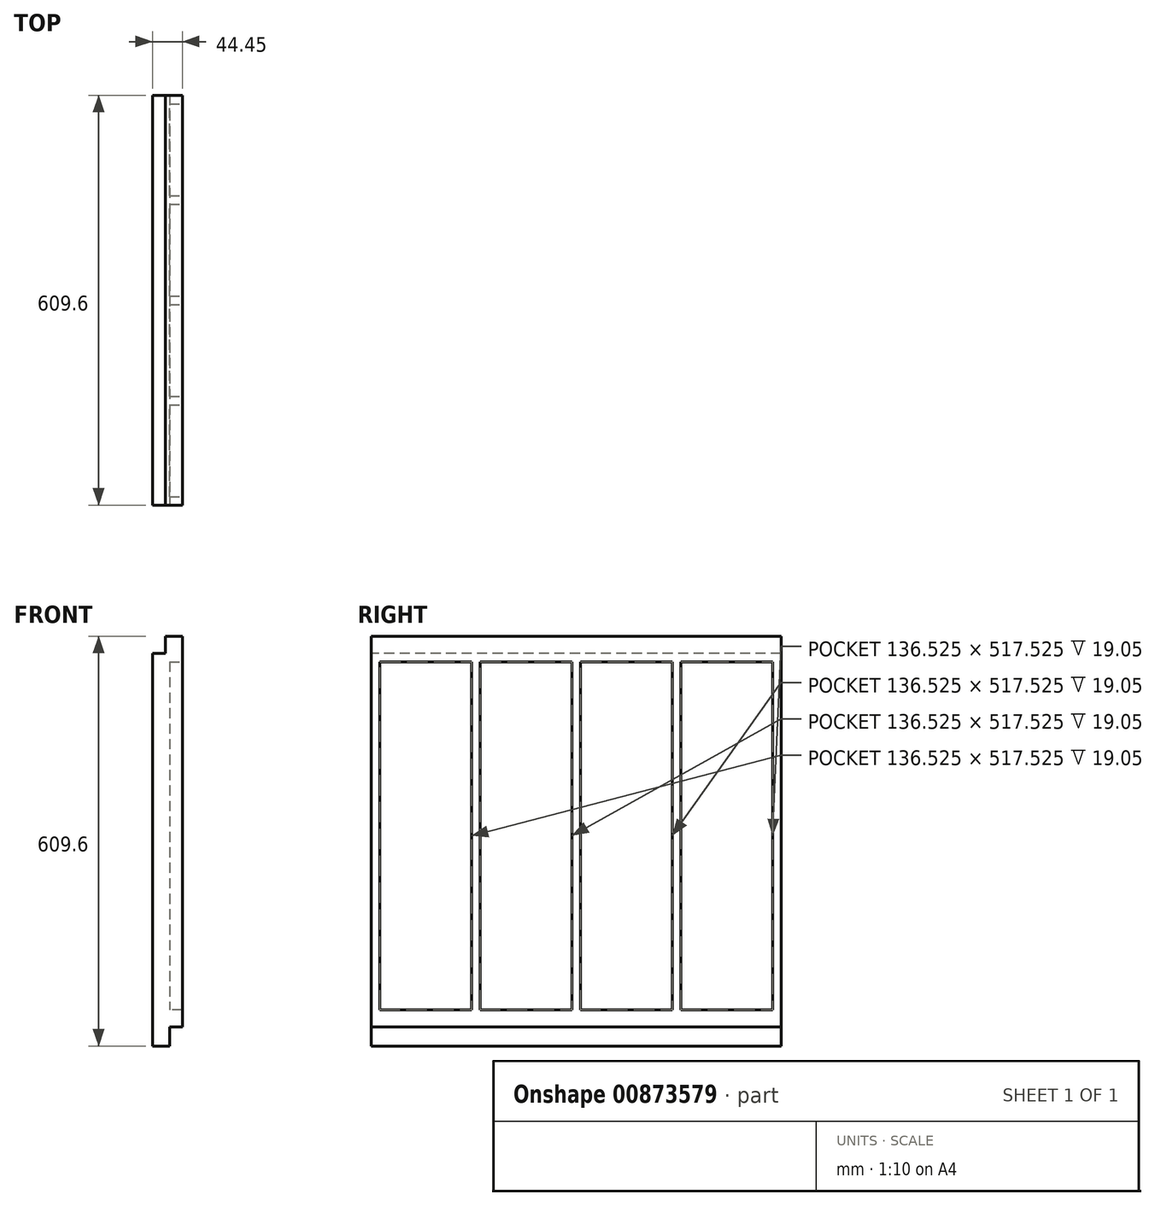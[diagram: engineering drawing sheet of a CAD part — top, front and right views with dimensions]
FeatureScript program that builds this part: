
annotation { "Feature Type Name" : "Feature", "Feature Type Description" : "" }
export const myFeature = defineFeature(function(context is Context, id is Id, definition is map)
    precondition{}
    {
        {
            var Q0;
            Q0=qCreatedBy(makeId("Top.planeOp"),FACE);
            var sketch = newSketch(context, id + "F0", { "sketchPlane" : qUnion([Q0])});
            skLineSegment(sketch, "E0.bottom", {"start": v(0, 0) * mm, "end": v(25.4, 0) * mm});
            skLineSegment(sketch, "E0.top", {"start": v(0, 609.6) * mm, "end": v(25.4, 609.6) * mm});
            skLineSegment(sketch, "E0.left", {"start": v(0, 0) * mm, "end": v(0, 609.6) * mm});
            skLineSegment(sketch, "E0.right", {"start": v(25.4, 12.7) * mm, "end": v(25.4, 149.23) * mm});
            skLineSegment(sketch, "E1", {"start": v(12.7, 648.7) * mm, "end": v(12.7, -109.72) * mm, "construction": true});
            skPoint(sketch, "E1.startSnap0", {"position": v(12.7, 609.6) * mm});
            skLineSegment(sketch, "E2.bottom", {"start": v(25.4, 0) * mm, "end": v(44.45, 0) * mm});
            skLineSegment(sketch, "E2.top", {"start": v(25.4, 12.7) * mm, "end": v(44.45, 12.7) * mm});
            skLineSegment(sketch, "E2.right", {"start": v(44.45, 0) * mm, "end": v(44.45, 12.7) * mm});
            skLineSegment(sketch, "E3.0.1.0", {"start": v(25.4, 161.93) * mm, "end": v(44.45, 161.93) * mm});
            skLineSegment(sketch, "E3.0.1.1", {"start": v(44.45, 149.23) * mm, "end": v(44.45, 161.93) * mm});
            skLineSegment(sketch, "E3.0.1.2", {"start": v(25.4, 149.23) * mm, "end": v(44.45, 149.23) * mm});
            skLineSegment(sketch, "E3.0.2.0", {"start": v(25.4, 311.15) * mm, "end": v(44.45, 311.15) * mm});
            skLineSegment(sketch, "E3.0.2.1", {"start": v(44.45, 298.45) * mm, "end": v(44.45, 311.15) * mm});
            skLineSegment(sketch, "E3.0.2.2", {"start": v(25.4, 298.45) * mm, "end": v(44.45, 298.45) * mm});
            skLineSegment(sketch, "E3.0.3.0", {"start": v(25.4, 460.38) * mm, "end": v(44.45, 460.38) * mm});
            skLineSegment(sketch, "E3.0.3.1", {"start": v(44.45, 447.68) * mm, "end": v(44.45, 460.38) * mm});
            skLineSegment(sketch, "E3.0.3.2", {"start": v(25.4, 447.68) * mm, "end": v(44.45, 447.68) * mm});
            skLineSegment(sketch, "E3.0.4.0", {"start": v(25.4, 609.6) * mm, "end": v(44.45, 609.6) * mm});
            skLineSegment(sketch, "E3.0.4.1", {"start": v(44.45, 596.9) * mm, "end": v(44.45, 609.6) * mm});
            skLineSegment(sketch, "E3.0.4.2", {"start": v(25.4, 596.9) * mm, "end": v(44.45, 596.9) * mm});
            skLineSegment(sketch, "E3.direction1", {"start": v(25.4, 12.7) * mm, "end": v(50.8, 12.7) * mm, "construction": true});
            skLineSegment(sketch, "E3.direction2", {"start": v(25.4, 12.7) * mm, "end": v(25.4, 149.22) * mm, "construction": true});
            skLineSegment(sketch, "E4.trimOffspring", {"start": v(25.4, 460.38) * mm, "end": v(25.4, 596.9) * mm});
            skLineSegment(sketch, "E5.trimOffspring", {"start": v(25.4, 311.15) * mm, "end": v(25.4, 447.68) * mm});
            skLineSegment(sketch, "E6.trimOffspring", {"start": v(25.4, 161.93) * mm, "end": v(25.4, 298.45) * mm});
            skSolve(sketch);
        }
        {
            var Q0;
            Q0 = qSketchRegion(id + "F0", true);
            extrude(context, id + "F1", {"entities" : qUnion([Q0]), "depth" : 609.6 * mm, "offsetDistance" : 25.4 * mm});
        }
        {
            var Q0;
            Q0=makeQuery(id+"F1.opExtrude","SWEPT_FACE",FACE,{"disambiguationData":[OSD([sQuery(id+"F0.wireOp",EDGE,"E0.bottom"),sQuery(id+"F0.wireOp",EDGE,"E2.bottom")])]});
            var sketch = newSketch(context, id + "F2", { "sketchPlane" : qUnion([Q0])});
            skLineSegment(sketch, "E7.bottom", {"start": v(0, 0) * mm, "end": v(50.8, 0) * mm});
            skLineSegment(sketch, "E7.top", {"start": v(0, 25.4) * mm, "end": v(50.8, 25.4) * mm});
            skLineSegment(sketch, "E7.left", {"start": v(0, 0) * mm, "end": v(0, 25.4) * mm});
            skLineSegment(sketch, "E7.right", {"start": v(50.8, 0) * mm, "end": v(50.8, 25.4) * mm});
            skSolve(sketch);
        }
        {
            var Q0;
            Q0 = qSketchRegion(id + "F2", true);
            extrude(context, id + "F3", {"entities" : qUnion([Q0]), "operationType" : NewBodyOperationType.ADD, "oppositeDirection" : true, "depth" : 609.6 * mm, "offsetDistance" : 25.4 * mm});
        }
        {
            var Q0;
            Q0=makeQuery(id+"F1.opExtrude","SWEPT_FACE",FACE,{"disambiguationData":[OSD([sQuery(id+"F0.wireOp",EDGE,"E0.bottom"),sQuery(id+"F0.wireOp",EDGE,"E2.bottom")])]});
            var sketch = newSketch(context, id + "F4", { "sketchPlane" : qUnion([Q0])});
            skLineSegment(sketch, "E8.bottom", {"start": v(0, 609.6) * mm, "end": v(25.4, 609.6) * mm});
            skLineSegment(sketch, "E8.top", {"start": v(0, 584.2) * mm, "end": v(25.4, 584.2) * mm});
            skLineSegment(sketch, "E8.left", {"start": v(0, 609.6) * mm, "end": v(0, 584.2) * mm});
            skLineSegment(sketch, "E8.right", {"start": v(25.4, 609.6) * mm, "end": v(25.4, 584.2) * mm});
            skSolve(sketch);
        }
        {
            var Q0;
            Q0 = qSketchRegion(id + "F4", true);
            extrude(context, id + "F5", {"entities" : qUnion([Q0]), "operationType" : NewBodyOperationType.REMOVE, "oppositeDirection" : true, "depth" : 609.6 * mm, "offsetDistance" : 25.4 * mm});
        }
        {
            var Q0;
            Q0=makeQuery(id+"F1.opExtrude","SWEPT_FACE",FACE,{"disambiguationData":[OSD([sQuery(id+"F0.wireOp",EDGE,"E0.bottom"),sQuery(id+"F0.wireOp",EDGE,"E2.bottom")])]});
            var sketch = newSketch(context, id + "F6", { "sketchPlane" : qUnion([Q0])});
            skLineSegment(sketch, "E9.bottom", {"start": v(50.8, 0) * mm, "end": v(25.4, 0) * mm});
            skLineSegment(sketch, "E9.top", {"start": v(50.8, 28.57) * mm, "end": v(25.4, 28.57) * mm});
            skLineSegment(sketch, "E9.left", {"start": v(50.8, 0) * mm, "end": v(50.8, 28.58) * mm});
            skLineSegment(sketch, "E9.right", {"start": v(25.4, 0) * mm, "end": v(25.4, 28.57) * mm});
            skSolve(sketch);
        }
        {
            var Q0;
            Q0 = qSketchRegion(id + "F6", true);
            extrude(context, id + "F7", {"entities" : qUnion([Q0]), "operationType" : NewBodyOperationType.REMOVE, "oppositeDirection" : true, "depth" : 609.6 * mm, "offsetDistance" : 25.4 * mm});
        }
        {
            var Q0;
            Q0=makeQuery(id+"F1.opExtrude","SWEPT_FACE",FACE,{"disambiguationData":[OSD([sQuery(id+"F0.wireOp",EDGE,"E0.bottom"),sQuery(id+"F0.wireOp",EDGE,"E2.bottom")])]});
            var sketch = newSketch(context, id + "F8", { "sketchPlane" : qUnion([Q0])});
            skLineSegment(sketch, "E10.bottom", {"start": v(25.4, 28.57) * mm, "end": v(44.45, 28.57) * mm});
            skLineSegment(sketch, "E10.top", {"start": v(25.4, 53.98) * mm, "end": v(44.45, 53.98) * mm});
            skLineSegment(sketch, "E10.left", {"start": v(25.4, 28.57) * mm, "end": v(25.4, 53.97) * mm});
            skLineSegment(sketch, "E10.right", {"start": v(44.45, 28.57) * mm, "end": v(44.45, 53.97) * mm});
            skLineSegment(sketch, "E11.bottom", {"start": v(44.45, 609.6) * mm, "end": v(19.05, 609.6) * mm});
            skLineSegment(sketch, "E11.top", {"start": v(44.45, 571.5) * mm, "end": v(19.05, 571.5) * mm});
            skLineSegment(sketch, "E11.left", {"start": v(44.45, 609.6) * mm, "end": v(44.45, 571.5) * mm});
            skLineSegment(sketch, "E11.right", {"start": v(19.05, 609.6) * mm, "end": v(19.05, 571.5) * mm});
            skSolve(sketch);
        }
        {
            var Q0;
            Q0 = qSketchRegion(id + "F8", true);
            extrude(context, id + "F9", {"entities" : qUnion([Q0]), "operationType" : NewBodyOperationType.ADD, "oppositeDirection" : true, "depth" : 609.6 * mm, "offsetDistance" : 25.4 * mm});
        }
    });
